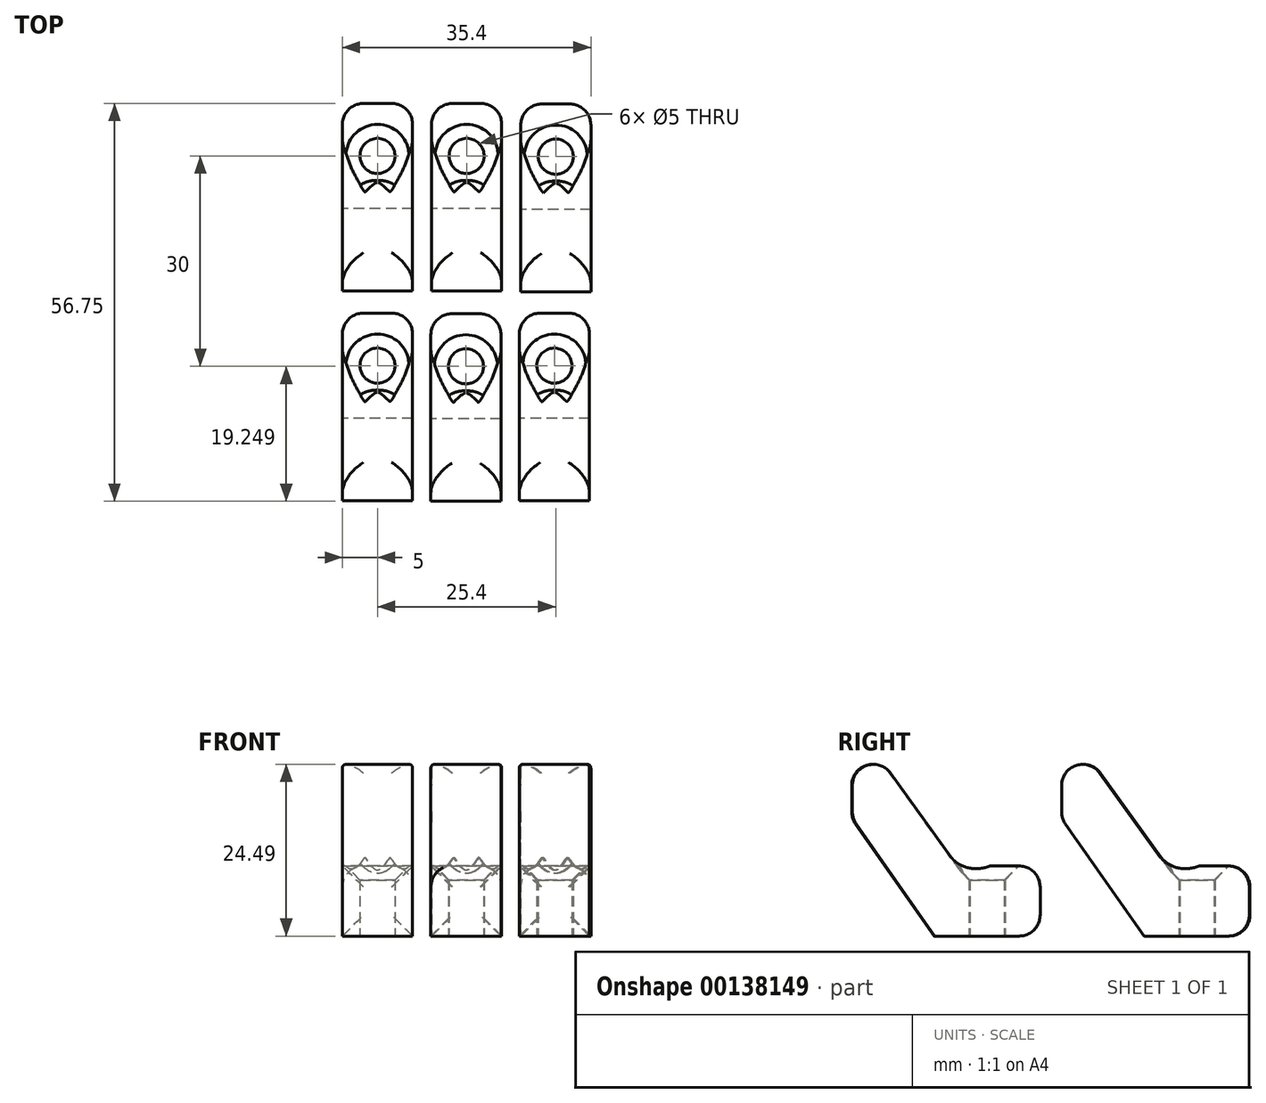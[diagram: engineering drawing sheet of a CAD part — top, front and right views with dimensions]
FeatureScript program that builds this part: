
annotation { "Feature Type Name" : "Feature", "Feature Type Description" : "" }
export const myFeature = defineFeature(function(context is Context, id is Id, definition is map)
    precondition{}
    {
        {
            var Q0;
            Q0=qCreatedBy(makeId("Right.planeOp"),FACE);
            var sketch = newSketch(context, id + "F0", { "sketchPlane" : qUnion([Q0])});
            skPoint(sketch, "E0", {"position": v(0, 16.78) * mm});
            skPoint(sketch, "E1", {"position": v(11.75, 0) * mm});
            skLineSegment(sketch, "E2", {"start": v(11.75, 0) * mm, "end": v(0, 16.78) * mm});
            skPoint(sketch, "E3", {"position": v(0, 30.78) * mm});
            skPoint(sketch, "E4", {"position": v(26.75, 10) * mm});
            skPoint(sketch, "E5", {"position": v(21.75, 0) * mm});
            skLineSegment(sketch, "E6", {"start": v(26.75, 10) * mm, "end": v(14.98, 10) * mm});
            skLineSegment(sketch, "E7", {"start": v(26.75, 10) * mm, "end": v(26.75, 0) * mm});
            skLineSegment(sketch, "E8", {"start": v(26.75, 0) * mm, "end": v(21.75, 0) * mm});
            skLineSegment(sketch, "E9", {"start": v(14.98, 10) * mm, "end": v(0, 30.78) * mm});
            skLineSegment(sketch, "E10", {"start": v(0, 16.78) * mm, "end": v(0, 30.78) * mm});
            skLineSegment(sketch, "E11", {"start": v(11.75, 0) * mm, "end": v(26.75, 0) * mm});
            skPoint(sketch, "E12", {"position": v(14.98, 10) * mm});
            skSolve(sketch);
        }
        {
            var Q0;
            {var subQ1=sQuery(id+"F0.wireOp",EDGE,"E2");Q0=makeQuery(id+"F0.imprint","IMPRINT",FACE,{"disambiguationData":[TD([[makeQuery(id+"F0.imprint","IMPRINT",EDGE,{"derivedFrom":subQ1}),-1.0]])]});}
            extrude(context, id + "F1", {"entities" : qUnion([Q0]), "depth" : 10 * mm});
        }
        {
            var Q0;
            Q0=qCreatedBy(makeId("Top.planeOp"),FACE);
            var sketch = newSketch(context, id + "F2", { "sketchPlane" : qUnion([Q0])});
            skCircle(sketch, "E13", {"center": v(5, 19.25) * mm, "radius": 2.5 * mm});
            skSolve(sketch);
        }
        {
            var Q0;
            Q0=makeQuery(id+"F2.imprint","IMPRINT",FACE,{"disambiguationData":[TD([[makeQuery(id+"F2.imprint","IMPRINT",EDGE,{"derivedFrom":sQuery(id+"F2.wireOp",EDGE,"E13")}),1.0]])]});
            extrude(context, id + "F3", {"entities" : qUnion([Q0]), "operationType" : NewBodyOperationType.REMOVE, "depth" : 16.1 * mm});
        }
        {
            var Q0;
            Q0=makeQuery(id+"F3.boolean.opBoolean","INTERSECT",EDGE,{"derivedFrom":[makeQuery(id+"F1.opExtrude","SWEPT_FACE",FACE,{"disambiguationData":[OSD([sQuery(id+"F0.wireOp",EDGE,"E6")])]}),makeQuery(id+"F3.opExtrude","SWEPT_FACE",FACE,{"disambiguationData":[OSD([sQuery(id+"F2.wireOp",EDGE,"E13")])]})]});
            chamfer(context, id + "F4", {"entities" : qUnion([Q0]), "width" : 2 * mm, "tangentPropagation" : true});
        }
        {
            var Q0;
            Q0=makeQuery(id+"F1.opExtrude","SWEPT_FACE",FACE,{"disambiguationData":[OSD([sQuery(id+"F0.wireOp",EDGE,"E9")])]});
            fillet(context, id + "F5", {"entities" : qUnion([Q0]), "radius" : 3 * mm, "tangentPropagation" : true, "allowEdgeOverflow" : false});
        }
        {
            var Q0;
            Q0=makeQuery(id+"F1.opExtrude","SWEPT_FACE",FACE,{"disambiguationData":[OSD([sQuery(id+"F0.wireOp",EDGE,"E7")])]});
            var Q1;
            Q1=makeQuery(id+"F1.opExtrude","SWEPT_EDGE",EDGE,{"disambiguationData":[OSD([sQuery(id+"F0.wireOp",EDGE,"E2"),sQuery(id+"F0.wireOp",EDGE,"E10")])]});
            fillet(context, id + "F6", {"entities" : qUnion([Q0, Q1]), "radius" : 3 * mm, "tangentPropagation" : true, "allowEdgeOverflow" : false});
        }
        {
            var Q0;
            Q0=makeQuery(id+"F1.opExtrude","SWEPT_BODY",BODY,{"disambiguationData":[OSD([sQuery(id+"F0.wireOp",EDGE,"E2"),sQuery(id+"F0.wireOp",EDGE,"E6"),sQuery(id+"F0.wireOp",EDGE,"E7"),sQuery(id+"F0.wireOp",EDGE,"E9"),sQuery(id+"F0.wireOp",EDGE,"E10"),sQuery(id+"F0.wireOp",EDGE,"E11")])]});
            transform(context, id + "F7", {"entities" : qUnion([Q0]), "transformType" : TransformType.TRANSLATION_3D, "dx" : -0.1 * mm, "dy" : -30 * mm, "dz" : 0 * mm, "makeCopy" : true});
        }
        {
            var Q0;
            Q0=makeQuery(id+"F1.opExtrude","SWEPT_BODY",BODY,{"disambiguationData":[OSD([sQuery(id+"F0.wireOp",EDGE,"E2"),sQuery(id+"F0.wireOp",EDGE,"E6"),sQuery(id+"F0.wireOp",EDGE,"E7"),sQuery(id+"F0.wireOp",EDGE,"E9"),sQuery(id+"F0.wireOp",EDGE,"E10"),sQuery(id+"F0.wireOp",EDGE,"E11")])]});
            transform(context, id + "F8", {"entities" : qUnion([Q0]), "transformType" : TransformType.TRANSLATION_3D, "dx" : -12.7 * mm, "dy" : 0 * mm, "dz" : 0 * mm, "makeCopy" : true});
        }
        {
            var Q0;
            Q0=makeQuery(id+"F7.opPattern","COPY",BODY,{"derivedFrom":makeQuery(id+"F1.opExtrude","SWEPT_BODY",BODY,{"disambiguationData":[OSD([sQuery(id+"F0.wireOp",EDGE,"E2"),sQuery(id+"F0.wireOp",EDGE,"E6"),sQuery(id+"F0.wireOp",EDGE,"E7"),sQuery(id+"F0.wireOp",EDGE,"E9"),sQuery(id+"F0.wireOp",EDGE,"E10"),sQuery(id+"F0.wireOp",EDGE,"E11")])]}),"instanceName":"1"});
            transform(context, id + "F9", {"entities" : qUnion([Q0]), "transformType" : TransformType.TRANSLATION_3D, "dx" : -12.6 * mm, "dy" : 0.1 * mm, "dz" : 0 * mm, "makeCopy" : true});
        }
        {
            var Q0;
            Q0=makeQuery(id+"F1.opExtrude","SWEPT_BODY",BODY,{"disambiguationData":[OSD([sQuery(id+"F0.wireOp",EDGE,"E2"),sQuery(id+"F0.wireOp",EDGE,"E6"),sQuery(id+"F0.wireOp",EDGE,"E7"),sQuery(id+"F0.wireOp",EDGE,"E9"),sQuery(id+"F0.wireOp",EDGE,"E10"),sQuery(id+"F0.wireOp",EDGE,"E11")])]});
            transform(context, id + "F10", {"entities" : qUnion([Q0]), "transformType" : TransformType.TRANSLATION_3D, "dx" : 12.7 * mm, "dy" : -0.1 * mm, "dz" : 0 * mm, "makeCopy" : true});
        }
        {
            var Q0;
            Q0=makeQuery(id+"F7.opPattern","COPY",BODY,{"derivedFrom":makeQuery(id+"F1.opExtrude","SWEPT_BODY",BODY,{"disambiguationData":[OSD([sQuery(id+"F0.wireOp",EDGE,"E2"),sQuery(id+"F0.wireOp",EDGE,"E6"),sQuery(id+"F0.wireOp",EDGE,"E7"),sQuery(id+"F0.wireOp",EDGE,"E9"),sQuery(id+"F0.wireOp",EDGE,"E10"),sQuery(id+"F0.wireOp",EDGE,"E11")])]}),"instanceName":"1"});
            transform(context, id + "F11", {"entities" : qUnion([Q0]), "transformType" : TransformType.TRANSLATION_3D, "dx" : 12.6 * mm, "dy" : 0.1 * mm, "dz" : 0 * mm, "makeCopy" : true});
        }
    });
